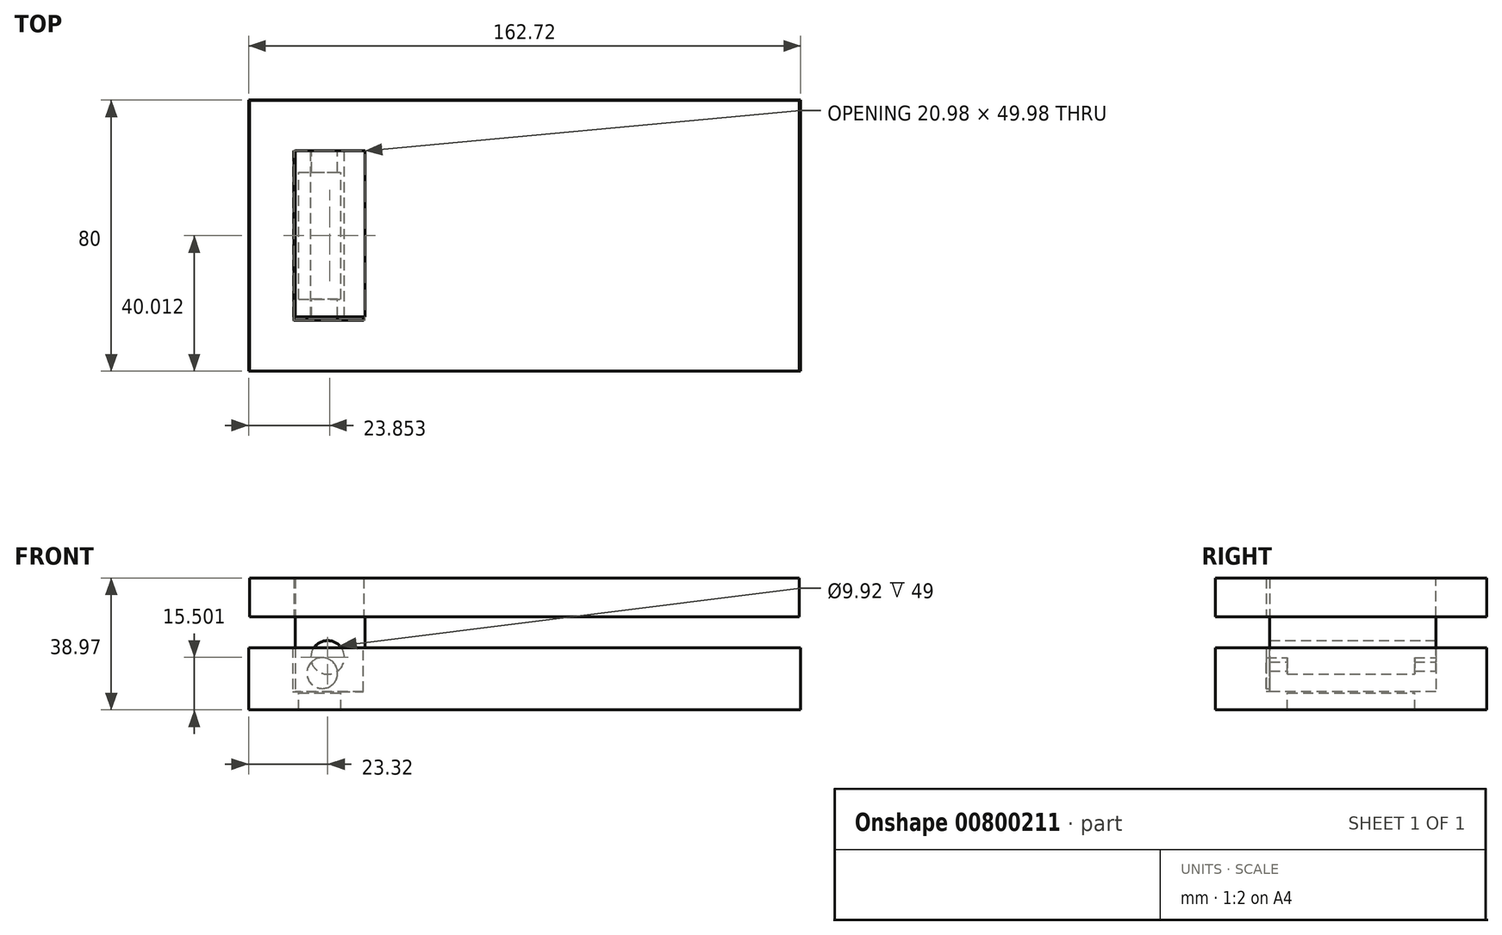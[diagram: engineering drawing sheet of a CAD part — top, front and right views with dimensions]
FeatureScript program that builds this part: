
annotation { "Feature Type Name" : "Feature", "Feature Type Description" : "" }
export const myFeature = defineFeature(function(context is Context, id is Id, definition is map)
    precondition{}
    {
        {
            var Q0;
            Q0=qCreatedBy(makeId("Front.planeOp"),FACE);
            var sketch = newSketch(context, id + "F0", { "sketchPlane" : qUnion([Q0])});
            skLineSegment(sketch, "E0.bottom", {"start": v(81.36, 9.19) * mm, "end": v(-81.36, 9.19) * mm});
            skLineSegment(sketch, "E0.top", {"start": v(81.36, -9.19) * mm, "end": v(-81.36, -9.19) * mm});
            skLineSegment(sketch, "E0.left", {"start": v(81.36, 9.19) * mm, "end": v(81.36, -9.19) * mm});
            skLineSegment(sketch, "E0.right", {"start": v(-81.36, 9.19) * mm, "end": v(-81.36, -9.19) * mm});
            skPoint(sketch, "E0.middle", {"position": v(0, 0) * mm});
            skSolve(sketch);
        }
        {
            var Q0;
            Q0 = qSketchRegion(id + "F0", true);
            extrude(context, id + "F1", {"entities" : qUnion([Q0]), "depth" : 40 * mm, "offsetDistance" : 25 * mm, "hasSecondDirection" : true, "secondDirectionOppositeDirection" : true, "secondDirectionDepth" : 40 * mm});
        }
        {
            var Q0;
            Q0=qCreatedBy(makeId("Front.planeOp"),FACE);
            var sketch = newSketch(context, id + "F2", { "sketchPlane" : qUnion([Q0])});
            skLineSegment(sketch, "E1.bottom", {"start": v(-68.32, 16.72) * mm, "end": v(-47.55, 16.72) * mm});
            skLineSegment(sketch, "E1.top", {"start": v(-68.32, -3.77) * mm, "end": v(-47.55, -3.77) * mm});
            skLineSegment(sketch, "E1.left", {"start": v(-68.32, 16.72) * mm, "end": v(-68.32, -3.77) * mm});
            skLineSegment(sketch, "E1.right", {"start": v(-47.55, 16.72) * mm, "end": v(-47.55, -3.77) * mm});
            skSolve(sketch);
        }
        {
            var Q0;
            Q0=makeQuery(id+"F2.imprint","IMPRINT",FACE,{"disambiguationData":[TD([[makeQuery(id+"F2.imprint","IMPRINT",EDGE,{"derivedFrom":sQuery(id+"F2.wireOp",EDGE,"E1.bottom")}),-1.0]])]});
            extrude(context, id + "F3", {"entities" : qUnion([Q0]), "operationType" : NewBodyOperationType.REMOVE, "oppositeDirection" : true, "depth" : 25 * mm, "offsetDistance" : 25 * mm, "hasSecondDirection" : true, "secondDirectionOppositeDirection" : false, "secondDirectionDepth" : 25 * mm});
        }
        {
            var Q0;
            Q0=qCreatedBy(makeId("Front.planeOp"),FACE);
            var sketch = newSketch(context, id + "F4", { "sketchPlane" : qUnion([Q0])});
            skCircle(sketch, "E2", {"center": v(-59.64, 1.69) * mm, "radius": 4.54 * mm});
            skSolve(sketch);
        }
        {
            var Q0;
            Q0=makeQuery(id+"F4.imprint","IMPRINT",FACE,{"disambiguationData":[TD([[makeQuery(id+"F4.imprint","IMPRINT",EDGE,{"derivedFrom":sQuery(id+"F4.wireOp",EDGE,"E2")}),1.0]])]});
            var Q1;
            Q1=sQuery(id+"F4.wireOp",EDGE,"E2");
            extrude(context, id + "F5", {"entities" : qUnion([Q0]), "operationType" : NewBodyOperationType.ADD, "surfaceOperationType" : NewSurfaceOperationType.ADD, "surfaceEntities" : qUnion([Q1]), "depth" : 25 * mm, "offsetDistance" : 25 * mm, "hasSecondDirection" : true, "secondDirectionOppositeDirection" : true, "secondDirectionDepth" : 25 * mm});
        }
        {
            var Q0;
            Q0=qCreatedBy(makeId("Top.planeOp"),FACE);
            var sketch = newSketch(context, id + "F6", { "sketchPlane" : qUnion([Q0])});
            skLineSegment(sketch, "E3.bottom", {"start": v(-54.13, 18.75) * mm, "end": v(-66.57, 18.75) * mm});
            skLineSegment(sketch, "E3.top", {"start": v(-54.13, -18.75) * mm, "end": v(-66.57, -18.75) * mm});
            skLineSegment(sketch, "E3.left", {"start": v(-54.13, 18.75) * mm, "end": v(-54.13, -18.75) * mm});
            skLineSegment(sketch, "E3.right", {"start": v(-66.57, 18.75) * mm, "end": v(-66.57, -18.75) * mm});
            skPoint(sketch, "E3.middle", {"position": v(-60.35, 0) * mm});
            skSolve(sketch);
        }
        {
            var Q0;
            Q0 = qSketchRegion(id + "F6", true);
            extrude(context, id + "F7", {"entities" : qUnion([Q0]), "operationType" : NewBodyOperationType.REMOVE, "oppositeDirection" : true, "depth" : 25 * mm, "offsetDistance" : 25 * mm, "hasSecondDirection" : true, "secondDirectionOppositeDirection" : false, "secondDirectionDepth" : 25 * mm});
        }
        {
            var Q0;
            Q0=qCreatedBy(makeId("Top.planeOp"),FACE);
            cPlane(context, id + "F8", {"entities" : qUnion([Q0]), "cplaneType" : CPlaneType.OFFSET, "offset" : 18.3 * mm, "width" : 150 * mm, "height" : 150 * mm});
        }
        {
            var Q0;
            Q0=qCreatedBy(id+"F8.planeOp",FACE);
            var sketch = newSketch(context, id + "F9", { "sketchPlane" : qUnion([Q0])});
            skLineSegment(sketch, "E4.bottom", {"start": v(81.05, 39.97) * mm, "end": v(-81.05, 39.97) * mm});
            skLineSegment(sketch, "E4.top", {"start": v(81.05, -39.97) * mm, "end": v(-81.05, -39.97) * mm});
            skLineSegment(sketch, "E4.left", {"start": v(81.05, 39.97) * mm, "end": v(81.05, -39.97) * mm});
            skLineSegment(sketch, "E4.right", {"start": v(-81.05, 39.97) * mm, "end": v(-81.05, -39.97) * mm});
            skPoint(sketch, "E4.middle", {"position": v(0, 0) * mm});
            skLineSegment(sketch, "E5.bottom", {"start": v(-47.37, 24.98) * mm, "end": v(-68, 24.98) * mm});
            skLineSegment(sketch, "E5.top", {"start": v(-47.37, -24.98) * mm, "end": v(-68, -24.98) * mm});
            skLineSegment(sketch, "E5.left", {"start": v(-47.37, 24.98) * mm, "end": v(-47.37, -24.98) * mm});
            skLineSegment(sketch, "E5.right", {"start": v(-68, 24.98) * mm, "end": v(-68, -24.98) * mm});
            skPoint(sketch, "E5.middle", {"position": v(-57.68, 0) * mm});
            skSolve(sketch);
        }
        {
            var Q0;
            Q0=makeQuery(id+"F9.imprint","IMPRINT",FACE,{"disambiguationData":[TD([[makeQuery(id+"F9.imprint","IMPRINT",EDGE,{"derivedFrom":sQuery(id+"F9.wireOp",EDGE,"E4.bottom")}),1.0]])]});
            extrude(context, id + "F10", {"entities" : qUnion([Q0]), "depth" : 11.4 * mm, "offsetDistance" : 25 * mm});
        }
        {
            var Q0;
            Q0=qCreatedBy(makeId("Front.planeOp"),FACE);
            var sketch = newSketch(context, id + "F11", { "sketchPlane" : qUnion([Q0])});
            skLineSegment(sketch, "E6.bottom", {"start": v(-67.64, 29.78) * mm, "end": v(-47.02, 29.78) * mm});
            skLineSegment(sketch, "E6.top", {"start": v(-67.64, -4.18) * mm, "end": v(-47.02, -4.18) * mm});
            skLineSegment(sketch, "E6.left", {"start": v(-67.64, 29.78) * mm, "end": v(-67.64, -4.18) * mm});
            skLineSegment(sketch, "E6.right", {"start": v(-47.02, 29.78) * mm, "end": v(-47.02, -4.18) * mm});
            skCircle(sketch, "E7", {"center": v(-58.04, 6.31) * mm, "radius": 4.96 * mm});
            skSolve(sketch);
        }
        {
            var Q0;
            Q0=makeQuery(id+"F11.imprint","IMPRINT",FACE,{"disambiguationData":[TD([[makeQuery(id+"F11.imprint","IMPRINT",EDGE,{"derivedFrom":sQuery(id+"F11.wireOp",EDGE,"E6.bottom")}),-1.0]])]});
            extrude(context, id + "F12", {"entities" : qUnion([Q0]), "operationType" : NewBodyOperationType.ADD, "depth" : 24 * mm, "offsetDistance" : 25 * mm, "hasSecondDirection" : true, "secondDirectionOppositeDirection" : true, "secondDirectionDepth" : 25 * mm});
        }
    });
